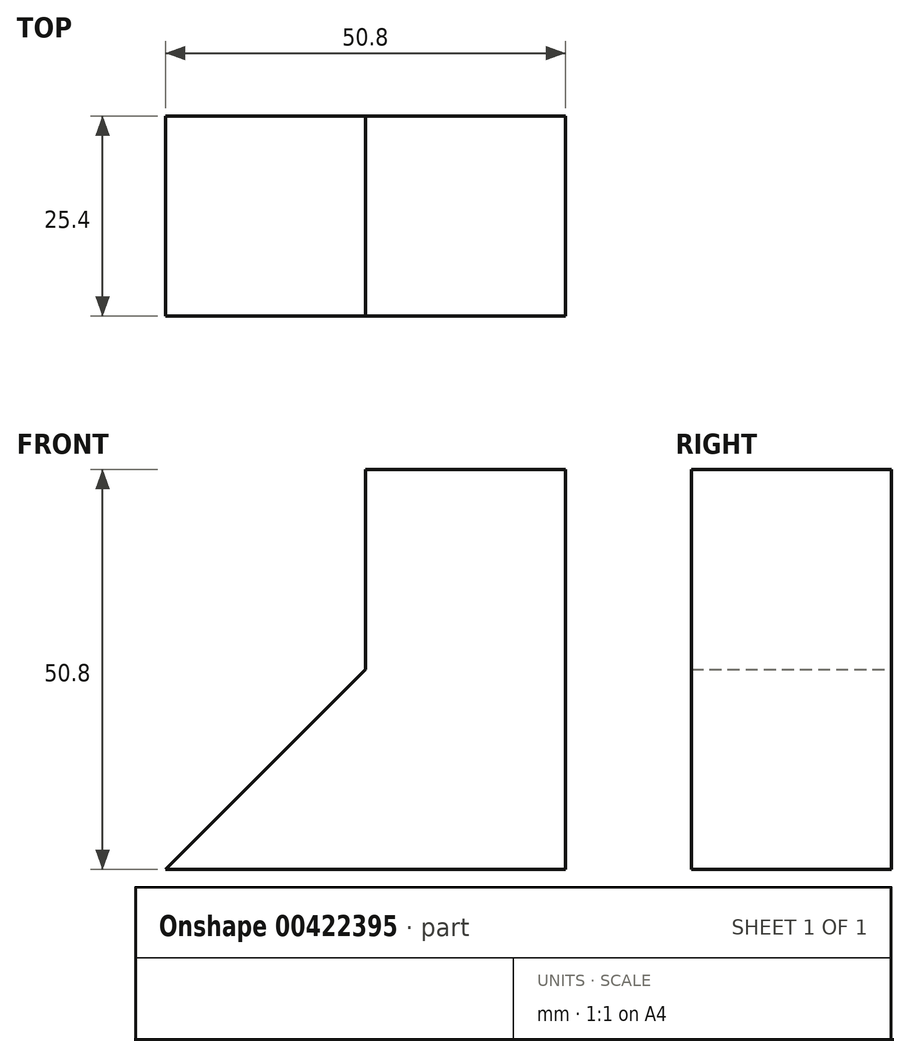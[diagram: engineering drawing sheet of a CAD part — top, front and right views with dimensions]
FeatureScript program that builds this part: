
annotation { "Feature Type Name" : "Feature", "Feature Type Description" : "" }
export const myFeature = defineFeature(function(context is Context, id is Id, definition is map)
    precondition{}
    {
        {
            var Q0;
            Q0=qCreatedBy(makeId("Front.planeOp"),FACE);
            var sketch = newSketch(context, id + "F0", { "sketchPlane" : qUnion([Q0])});
            skLineSegment(sketch, "E0", {"start": v(0, 0) * mm, "end": v(-50.8, 0) * mm});
            skLineSegment(sketch, "E1", {"start": v(0, 0) * mm, "end": v(0, 50.8) * mm});
            skLineSegment(sketch, "E2", {"start": v(0, 50.8) * mm, "end": v(-25.4, 50.8) * mm});
            skLineSegment(sketch, "E3", {"start": v(-25.4, 50.8) * mm, "end": v(-25.4, 25.4) * mm});
            skLineSegment(sketch, "E4", {"start": v(-25.4, 25.4) * mm, "end": v(-50.8, 0) * mm});
            skSolve(sketch);
        }
        {
            var Q0;
            Q0 = qSketchRegion(id + "F0", true);
            extrude(context, id + "F1", {"entities" : qUnion([Q0]), "depth" : 25.4 * mm});
        }
    });
